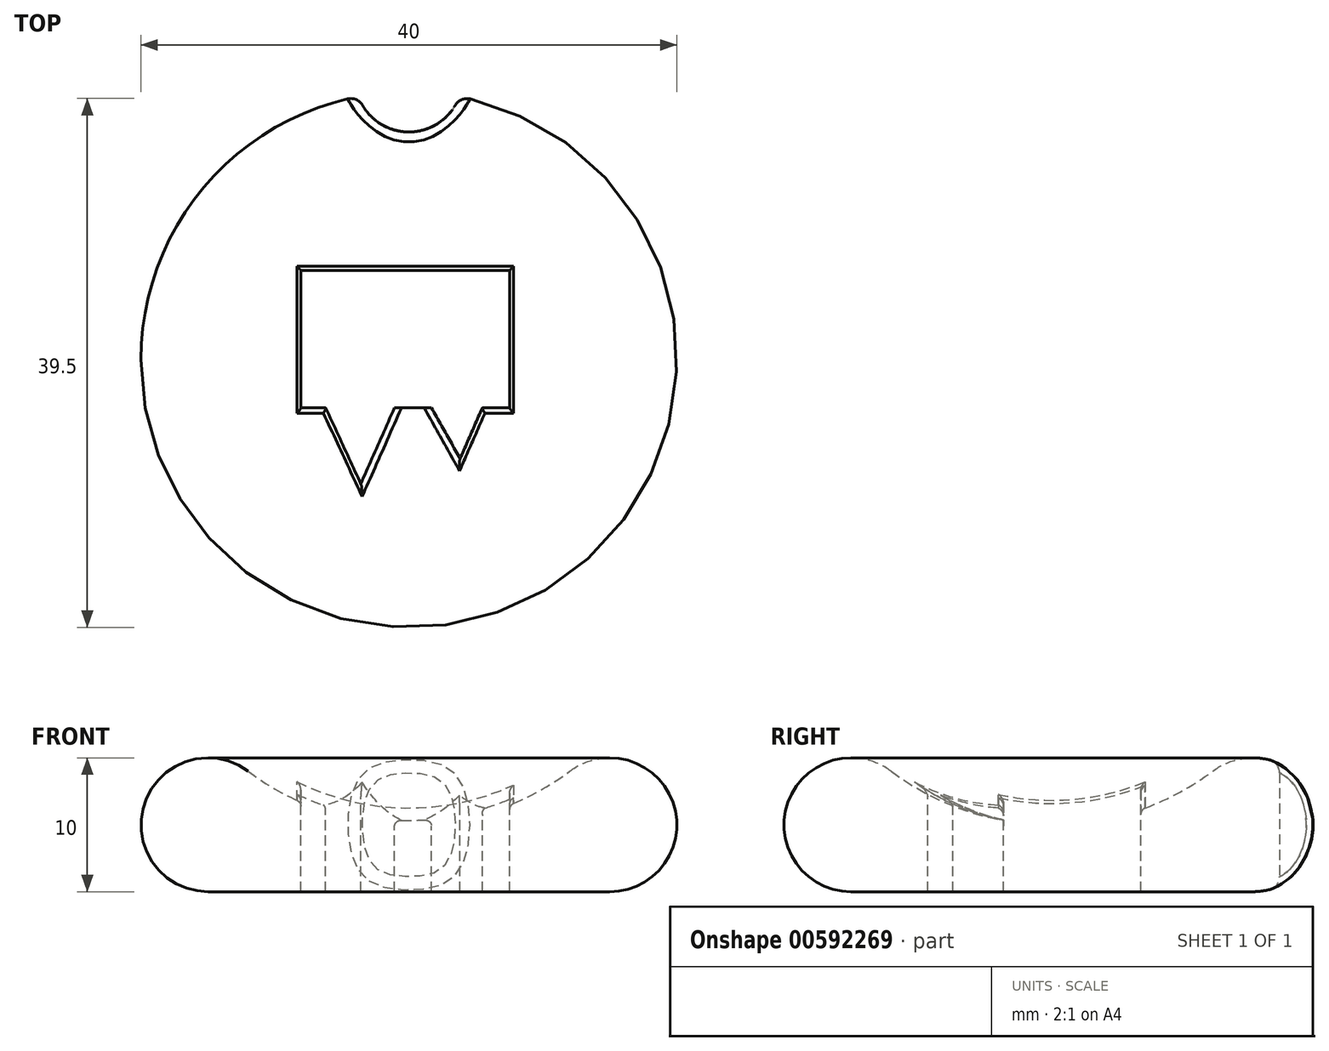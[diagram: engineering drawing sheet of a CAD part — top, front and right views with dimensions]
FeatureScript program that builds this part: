
annotation { "Feature Type Name" : "Feature", "Feature Type Description" : "" }
export const myFeature = defineFeature(function(context is Context, id is Id, definition is map)
    precondition{}
    {
        {
            var Q0;
            Q0=qCreatedBy(makeId("Right.planeOp"),FACE);
            var sketch = newSketch(context, id + "F0", { "sketchPlane" : qUnion([Q0])});
            skArc(sketch, "E0", {"start": v(-12, 9) * mm, "mid": v(-19.74, 6.58) * mm, "end": v(-15, 0) * mm});
            skArc(sketch, "E1", {"start": v(-12, 9) * mm, "mid": v(-6.32, 6.03) * mm, "end": v(0, 5) * mm});
            skLineSegment(sketch, "E2", {"start": v(-15, 0) * mm, "end": v(0, 0) * mm});
            skLineSegment(sketch, "E3", {"start": v(0, 0) * mm, "end": v(0, 5) * mm});
            skSolve(sketch);
        }
        {
            var Q0;
            Q0=makeQuery(id+"F0.imprint","IMPRINT",FACE,{"disambiguationData":[TD([[makeQuery(id+"F0.imprint","IMPRINT",EDGE,{"derivedFrom":sQuery(id+"F0.wireOp",EDGE,"E0")}),1.0]])]});
            var Q1;
            Q1=sQuery(id+"F0.wireOp",EDGE,"E3");
            revolve(context, id + "F1", {"entities" : qUnion([Q0]), "axis" : qUnion([Q1]), "revolveType" : RevolveType.FULL});
        }
        {
            var Q0;
            Q0=qCreatedBy(makeId("Top.planeOp"),FACE);
            cPlane(context, id + "F2", {"entities" : qUnion([Q0]), "cplaneType" : CPlaneType.OFFSET, "offset" : 9 * mm, "width" : 150 * mm, "height" : 150 * mm});
        }
        {
            var Q0;
            Q0=qCreatedBy(id+"F2.planeOp",FACE);
            var sketch = newSketch(context, id + "F3", { "sketchPlane" : qUnion([Q0])});
            skLineSegment(sketch, "E4.bottom", {"start": v(-8.06, 6.64) * mm, "end": v(7.52, 6.64) * mm});
            skLineSegment(sketch, "E4.top", {"start": v(-8.06, -3.6) * mm, "end": v(7.52, -3.6) * mm});
            skLineSegment(sketch, "E4.left", {"start": v(-8.06, 6.64) * mm, "end": v(-8.06, -3.6) * mm});
            skLineSegment(sketch, "E4.right", {"start": v(7.52, 6.64) * mm, "end": v(7.52, -3.6) * mm});
            skLineSegment(sketch, "E5", {"start": v(-6.21, -3.6) * mm, "end": v(-3.59, -9.28) * mm});
            skLineSegment(sketch, "E6", {"start": v(-3.59, -9.28) * mm, "end": v(-1.07, -3.6) * mm});
            skLineSegment(sketch, "E7", {"start": v(-1.07, -3.6) * mm, "end": v(1.69, -3.6) * mm});
            skLineSegment(sketch, "E8", {"start": v(1.69, -3.6) * mm, "end": v(3.83, -7.4) * mm});
            skLineSegment(sketch, "E9", {"start": v(3.83, -7.4) * mm, "end": v(5.48, -3.6) * mm});
            skSolve(sketch);
        }
        {
            var Q0;
            {var subQ0=sQuery(id+"F3.wireOp",EDGE,"E5");Q0=makeQuery(id+"F3.imprint","IMPRINT",FACE,{"disambiguationData":[TD([[makeQuery(id+"F3.imprint","IMPRINT",EDGE,{"derivedFrom":subQ0}),1.0]])]});}
            var Q1;
            {var subQ0=sQuery(id+"F3.wireOp",EDGE,"E8");Q1=makeQuery(id+"F3.imprint","IMPRINT",FACE,{"disambiguationData":[TD([[makeQuery(id+"F3.imprint","IMPRINT",EDGE,{"derivedFrom":subQ0}),1.0]])]});}
            var Q2;
            Q2=makeQuery(id+"F3.imprint","IMPRINT",FACE,{"disambiguationData":[TD([[makeQuery(id+"F3.imprint","IMPRINT",EDGE,{"derivedFrom":sQuery(id+"F3.wireOp",EDGE,"E4.bottom")}),-1.0]])]});
            extrude(context, id + "F4", {"entities" : qUnion([Q0, Q1, Q2]), "operationType" : NewBodyOperationType.REMOVE, "oppositeDirection" : true, "depth" : 25 * mm, "offsetDistance" : 25 * mm});
        }
        {
            var Q0;
            Q0=makeQuery(id+"F4.boolean.opBoolean","INTERSECT",EDGE,{"derivedFrom":[makeQuery(id+"F1.opRevolve","SWEPT_FACE",FACE,{"disambiguationData":[OSD([sQuery(id+"F0.wireOp",EDGE,"E1")])]}),makeQuery(id+"F4.opExtrude","SWEPT_FACE",FACE,{"disambiguationData":[OSD([sQuery(id+"F3.wireOp",EDGE,"E4.left")])]})]});
            var Q1;
            {var subQ0=sQuery(id+"F3.wireOp",EDGE,"E4.top");Q1=makeQuery(id+"F4.boolean.opBoolean","INTERSECT",EDGE,{"derivedFrom":[makeQuery(id+"F1.opRevolve","SWEPT_FACE",FACE,{"disambiguationData":[OSD([sQuery(id+"F0.wireOp",EDGE,"E1")])]}),makeQuery(id+"F4.opExtrude","SWEPT_FACE",FACE,{"disambiguationData":[OSD([subQ0]),TDD([makeQuery(id+"F3.imprint","IMPRINT",EDGE,{"disambiguationData":[TD([[makeQuery(id+"F3.imprint","INTERSECT",VERTEX,{"derivedFrom":[subQ0,sQuery(id+"F3.wireOp",EDGE,"E4.left")]}),-1.0]])],"derivedFrom":subQ0})])]})]});}
            var Q2;
            Q2=makeQuery(id+"F4.boolean.opBoolean","INTERSECT",EDGE,{"derivedFrom":[makeQuery(id+"F1.opRevolve","SWEPT_FACE",FACE,{"disambiguationData":[OSD([sQuery(id+"F0.wireOp",EDGE,"E1")])]}),makeQuery(id+"F4.opExtrude","SWEPT_FACE",FACE,{"disambiguationData":[OSD([sQuery(id+"F3.wireOp",EDGE,"E5")])]})]});
            var Q3;
            Q3=makeQuery(id+"F4.boolean.opBoolean","INTERSECT",EDGE,{"derivedFrom":[makeQuery(id+"F1.opRevolve","SWEPT_FACE",FACE,{"disambiguationData":[OSD([sQuery(id+"F0.wireOp",EDGE,"E1")])]}),makeQuery(id+"F4.opExtrude","SWEPT_FACE",FACE,{"disambiguationData":[OSD([sQuery(id+"F3.wireOp",EDGE,"E6")])]})]});
            var Q4;
            Q4=makeQuery(id+"F4.boolean.opBoolean","INTERSECT",EDGE,{"derivedFrom":[makeQuery(id+"F1.opRevolve","SWEPT_FACE",FACE,{"disambiguationData":[OSD([sQuery(id+"F0.wireOp",EDGE,"E1")])]}),makeQuery(id+"F4.opExtrude","SWEPT_FACE",FACE,{"disambiguationData":[OSD([sQuery(id+"F3.wireOp",EDGE,"E4.bottom")])]})]});
            var Q5;
            Q5=makeQuery(id+"F4.boolean.opBoolean","INTERSECT",EDGE,{"derivedFrom":[makeQuery(id+"F1.opRevolve","SWEPT_FACE",FACE,{"disambiguationData":[OSD([sQuery(id+"F0.wireOp",EDGE,"E1")])]}),makeQuery(id+"F4.opExtrude","SWEPT_FACE",FACE,{"disambiguationData":[OSD([sQuery(id+"F3.wireOp",EDGE,"E7")])]})]});
            var Q6;
            Q6=makeQuery(id+"F4.boolean.opBoolean","INTERSECT",EDGE,{"derivedFrom":[makeQuery(id+"F1.opRevolve","SWEPT_FACE",FACE,{"disambiguationData":[OSD([sQuery(id+"F0.wireOp",EDGE,"E1")])]}),makeQuery(id+"F4.opExtrude","SWEPT_FACE",FACE,{"disambiguationData":[OSD([sQuery(id+"F3.wireOp",EDGE,"E8")])]})]});
            var Q7;
            Q7=makeQuery(id+"F4.boolean.opBoolean","INTERSECT",EDGE,{"derivedFrom":[makeQuery(id+"F1.opRevolve","SWEPT_FACE",FACE,{"disambiguationData":[OSD([sQuery(id+"F0.wireOp",EDGE,"E1")])]}),makeQuery(id+"F4.opExtrude","SWEPT_FACE",FACE,{"disambiguationData":[OSD([sQuery(id+"F3.wireOp",EDGE,"E9")])]})]});
            var Q8;
            Q8=makeQuery(id+"F4.boolean.opBoolean","INTERSECT",EDGE,{"derivedFrom":[makeQuery(id+"F1.opRevolve","SWEPT_FACE",FACE,{"disambiguationData":[OSD([sQuery(id+"F0.wireOp",EDGE,"E1")])]}),makeQuery(id+"F4.opExtrude","SWEPT_FACE",FACE,{"disambiguationData":[OSD([sQuery(id+"F3.wireOp",EDGE,"E4.right")])]})]});
            var Q9;
            {var subQ0=sQuery(id+"F3.wireOp",EDGE,"E4.top");Q9=makeQuery(id+"F4.boolean.opBoolean","INTERSECT",EDGE,{"derivedFrom":[makeQuery(id+"F1.opRevolve","SWEPT_FACE",FACE,{"disambiguationData":[OSD([sQuery(id+"F0.wireOp",EDGE,"E1")])]}),makeQuery(id+"F4.opExtrude","SWEPT_FACE",FACE,{"disambiguationData":[OSD([subQ0]),TDD([makeQuery(id+"F3.imprint","IMPRINT",EDGE,{"disambiguationData":[TD([[makeQuery(id+"F3.imprint","INTERSECT",VERTEX,{"derivedFrom":[subQ0,sQuery(id+"F3.wireOp",EDGE,"E4.right")]}),1.0]])],"derivedFrom":subQ0})])]})]});}
            fillet(context, id + "F5", {"entities" : qUnion([Q0, Q1, Q2, Q3, Q4, Q5, Q6, Q7, Q8, Q9]), "radius" : .5 * mm, "tangentPropagation" : true, "allowEdgeOverflow" : false});
        }
        {
            var Q0;
            Q0=qCreatedBy(makeId("Top.planeOp"),FACE);
            var sketch = newSketch(context, id + "F6", { "sketchPlane" : qUnion([Q0])});
            skCircle(sketch, "E10", {"center": v(0, 21) * mm, "radius": 4 * mm});
            skSolve(sketch);
        }
        {
            var Q0;
            Q0 = qSketchRegion(id + "F6", true);
            extrude(context, id + "F7", {"entities" : qUnion([Q0]), "operationType" : NewBodyOperationType.REMOVE, "depth" : 29.4 * mm, "offsetDistance" : 25 * mm});
        }
        {
            var Q0;
            Q0=makeQuery(id+"F7.boolean.opBoolean","INTERSECT",EDGE,{"derivedFrom":[makeQuery(id+"F1.opRevolve","SWEPT_FACE",FACE,{"disambiguationData":[OSD([sQuery(id+"F0.wireOp",EDGE,"E0")])]}),makeQuery(id+"F7.opExtrude","SWEPT_FACE",FACE,{"disambiguationData":[OSD([sQuery(id+"F6.wireOp",EDGE,"E10")])]})]});
            fillet(context, id + "F8", {"entities" : qUnion([Q0]), "radius" : 1 * mm, "tangentPropagation" : true, "allowEdgeOverflow" : false});
        }
    });
